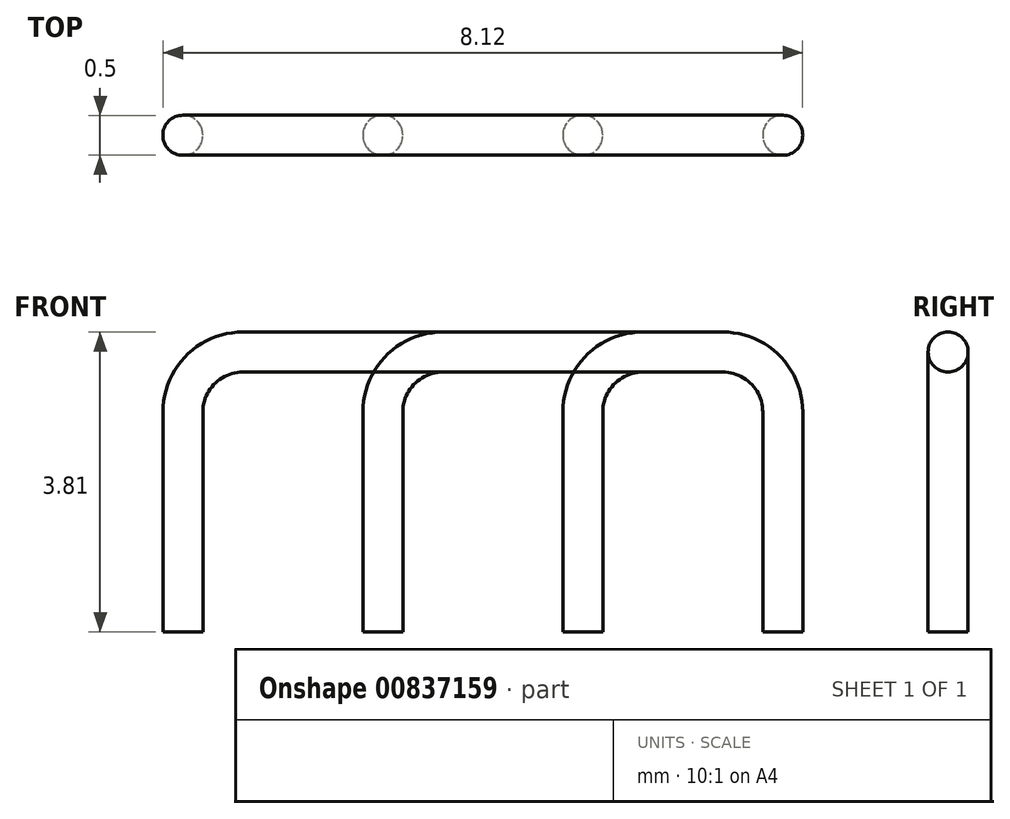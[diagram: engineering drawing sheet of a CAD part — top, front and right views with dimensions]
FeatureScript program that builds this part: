
annotation { "Feature Type Name" : "Feature", "Feature Type Description" : "" }
export const myFeature = defineFeature(function(context is Context, id is Id, definition is map)
    precondition{}
    {
        {
            var Q0;
            Q0=qCreatedBy(makeId("Front.planeOp"),FACE);
            var sketch = newSketch(context, id + "F0", { "sketchPlane" : qUnion([Q0])});
            skLineSegment(sketch, "E0", {"start": v(0, -2.54) * mm, "end": v(0, 0.25) * mm});
            skLineSegment(sketch, "E1", {"start": v(-5.08, 0.25) * mm, "end": v(-5.08, -2.54) * mm});
            skLineSegment(sketch, "E2", {"start": v(-5.08, -2.54) * mm, "end": v(0, -2.54) * mm, "construction": true});
            skLineSegment(sketch, "E3", {"start": v(0, 0.25) * mm, "end": v(-5.08, 0.25) * mm, "construction": true});
            skLineSegment(sketch, "E4", {"start": v(-4.32, 1.02) * mm, "end": v(-0.76, 1.02) * mm});
            skArc(sketch, "E5", {"start": v(0, 0.25) * mm, "mid": v(-0.22, 0.8) * mm, "end": v(-0.76, 1.02) * mm});
            skArc(sketch, "E6", {"start": v(-4.32, 1.02) * mm, "mid": v(-4.86, 0.8) * mm, "end": v(-5.08, 0.25) * mm});
            skSolve(sketch);
        }
        {
            var Q0;
            Q0=qCreatedBy(makeId("Top.planeOp"),FACE);
            cPlane(context, id + "F1", {"entities" : qUnion([Q0]), "cplaneType" : CPlaneType.OFFSET, "offset" : 2.54 * mm, "oppositeDirection" : true, "width" : 152.4 * mm, "height" : 152.4 * mm});
        }
        {
            var Q0;
            Q0=qCreatedBy(id+"F1.planeOp",FACE);
            var sketch = newSketch(context, id + "F2", { "sketchPlane" : qUnion([Q0])});
            skCircle(sketch, "E7", {"center": v(0, 0) * mm, "radius": 0.25 * mm});
            skSolve(sketch);
        }
        {
            var Q0;
            Q0=qSketchRegion(id+"F2",true);
            var Q1;
            Q1=qConstructionFilter(qBodyType(qCreatedBy(id+"F0",EDGE),BodyType.WIRE),ConstructionObject.NO);
            sweep(context, id + "F3", {"profiles" : qUnion([Q0]), "path" : qUnion([Q1])});
        }
        {
            var Q0;
            Q0=qCreatedBy(makeId("Front.planeOp"),FACE);
            var sketch = newSketch(context, id + "F4", { "sketchPlane" : qUnion([Q0])});
            skLineSegment(sketch, "E8", {"start": v(0, -2.54) * mm, "end": v(0, 0.25) * mm});
            skLineSegment(sketch, "E9", {"start": v(-7.62, 0.25) * mm, "end": v(-7.62, -2.54) * mm});
            skLineSegment(sketch, "E10", {"start": v(-7.62, -2.54) * mm, "end": v(0, -2.54) * mm, "construction": true});
            skLineSegment(sketch, "E11", {"start": v(0, 0.25) * mm, "end": v(-7.62, 0.25) * mm, "construction": true});
            skLineSegment(sketch, "E12", {"start": v(-6.86, 1.02) * mm, "end": v(-0.76, 1.02) * mm});
            skArc(sketch, "E13", {"start": v(0, 0.25) * mm, "mid": v(-0.22, 0.8) * mm, "end": v(-0.76, 1.02) * mm});
            skArc(sketch, "E14", {"start": v(-6.86, 1.02) * mm, "mid": v(-7.4, 0.8) * mm, "end": v(-7.62, 0.25) * mm});
            skSolve(sketch);
        }
        {
            var Q0;
            Q0 = qSketchRegion(id + "F2", true);
            var Q1;
            Q1 = qConstructionFilter(qBodyType(qCreatedBy(id + "F4" ,EDGE), BodyType.WIRE), ConstructionObject.NO);
            sweep(context, id + "F5", {"profiles" : qUnion([Q0]), "path" : qUnion([Q1])});
        }
        {
            var Q0;
            Q0=qCreatedBy(makeId("Front.planeOp"),FACE);
            var sketch = newSketch(context, id + "F6", { "sketchPlane" : qUnion([Q0])});
            skLineSegment(sketch, "E15", {"start": v(0, -2.54) * mm, "end": v(0, 0.25) * mm});
            skLineSegment(sketch, "E16", {"start": v(-2.54, 0.25) * mm, "end": v(-2.54, -2.54) * mm});
            skLineSegment(sketch, "E17", {"start": v(-2.54, -2.54) * mm, "end": v(0, -2.54) * mm, "construction": true});
            skLineSegment(sketch, "E18", {"start": v(0, 0.25) * mm, "end": v(-2.54, 0.25) * mm, "construction": true});
            skLineSegment(sketch, "E19", {"start": v(-1.78, 1.02) * mm, "end": v(-0.76, 1.02) * mm});
            skArc(sketch, "E20", {"start": v(0, 0.25) * mm, "mid": v(-0.22, 0.8) * mm, "end": v(-0.76, 1.02) * mm});
            skArc(sketch, "E21", {"start": v(-1.78, 1.02) * mm, "mid": v(-2.32, 0.8) * mm, "end": v(-2.54, 0.25) * mm});
            skSolve(sketch);
        }
        {
            var Q0;
            Q0 = qSketchRegion(id + "F2", true);
            var Q1;
            Q1 = qConstructionFilter(qBodyType(qCreatedBy(id + "F6" ,EDGE), BodyType.WIRE), ConstructionObject.NO);
            sweep(context, id + "F7", {"profiles" : qUnion([Q0]), "path" : qUnion([Q1])});
        }
    });
